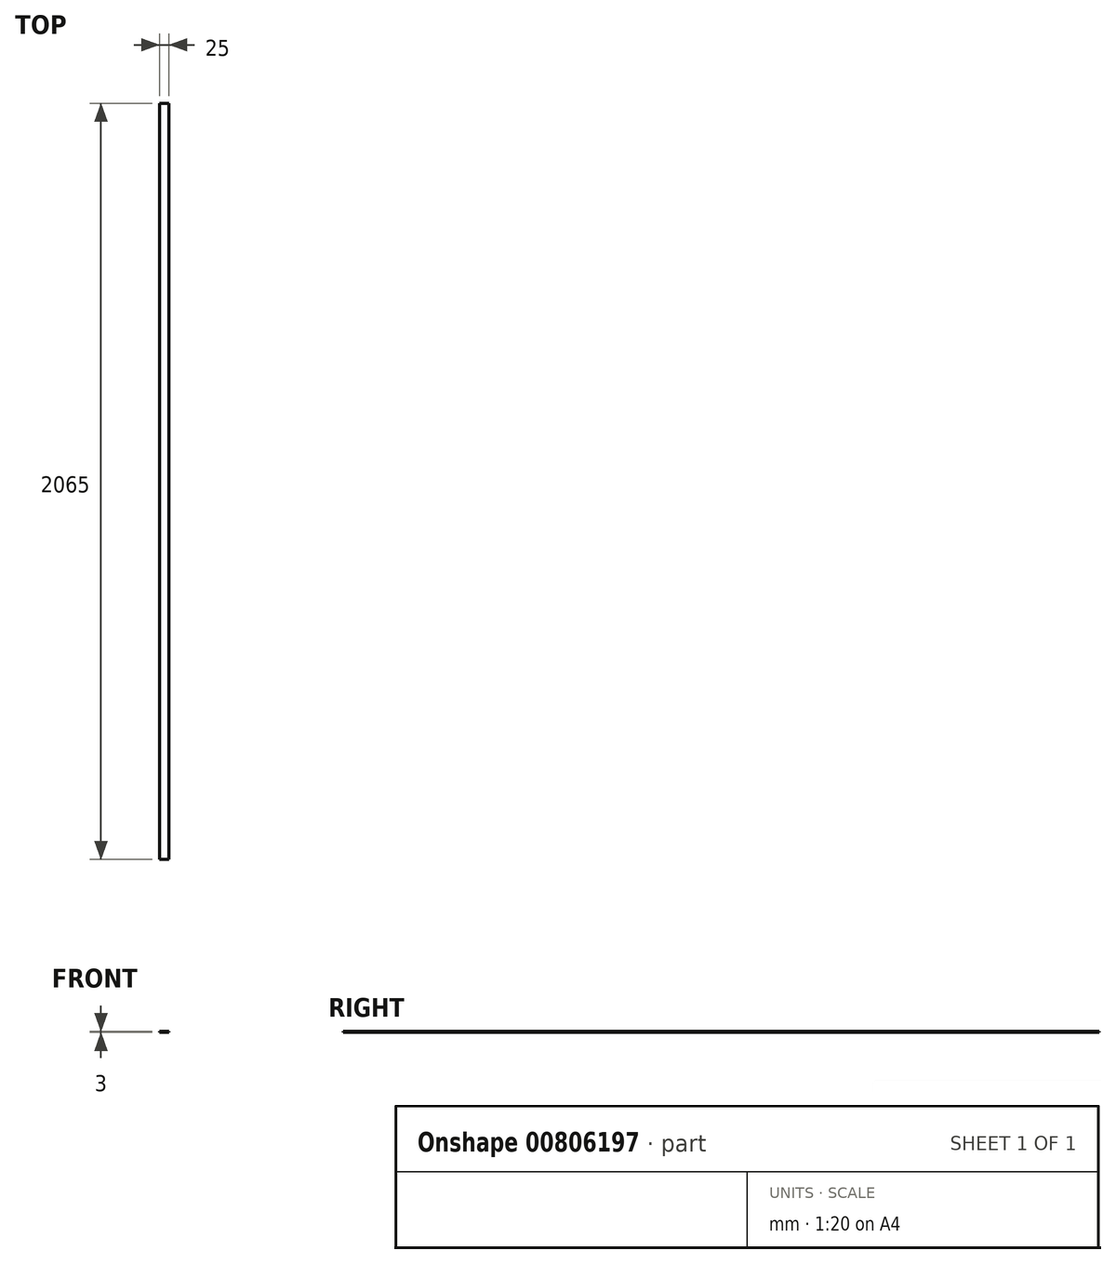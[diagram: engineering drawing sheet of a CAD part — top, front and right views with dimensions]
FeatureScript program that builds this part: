
annotation { "Feature Type Name" : "Feature", "Feature Type Description" : "" }
export const myFeature = defineFeature(function(context is Context, id is Id, definition is map)
    precondition{}
    {
        {
            var Q0;
            Q0=qCreatedBy(makeId("Front.planeOp"),FACE);
            var sketch = newSketch(context, id + "F0", { "sketchPlane" : qUnion([Q0])});
            skLineSegment(sketch, "E0.bottom", {"start": v(0, 0) * mm, "end": v(25, 0) * mm});
            skLineSegment(sketch, "E0.top", {"start": v(0, -3) * mm, "end": v(25, -3) * mm});
            skLineSegment(sketch, "E0.left", {"start": v(0, 0) * mm, "end": v(0, -3) * mm});
            skLineSegment(sketch, "E0.right", {"start": v(25, 0) * mm, "end": v(25, -3) * mm});
            skSolve(sketch);
        }
        {
            var Q0;
            Q0=qSketchRegion(id+"F0",true);
            extrude(context, id + "F1", {"entities" : qUnion([Q0]), "depth" : 2065 * mm, "offsetDistance" : 25 * mm});
        }
    });
